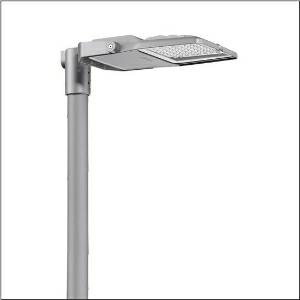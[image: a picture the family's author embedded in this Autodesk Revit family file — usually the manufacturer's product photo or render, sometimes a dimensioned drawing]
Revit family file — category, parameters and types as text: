
# Revit family: floodlight_fl_21_iq_mini___pl52_5xa7771d2d3a_64cb
name_source: partatom
category: Lighting Fixtures
units: mm (PartAtom-declared; Revit-internal decimal feet)

## family parameters
Cut with Voids When Loaded = No
Host = Face
Light Source = No
Part Type = Normal
Room Calculation Point = No
Round Connector Dimension = Use Diameter
Shared = No

## types (1)
- --- (1 x LED, 17830 lm, 143 W, 3000K)
    Apparent Load = 143 VA
    CIE Flux Codes = 26 60 98 100 100
    Color Rendering = 70
    Color Temperature = 3000K
    Default Elevation = 1800 mm
    Description = Floodlight FL 21 iQ mini, floodlight, primary light control with lens, of PMMA, primary optical cover: protective disc, of toughened safety glass, transparent, light distribution: PL52, light emission: direct distribution, installation type: surface-mounted, LED, High Power LED, rated luminous flux: 17.830lm, luminous efficacy: 125lm/W, light colour: 730, colour temperature: 3000K, control gear: iQ Comfort/DALI, control: Auto-Match, Temp-Guard, Lumen-Switch, Night-Set, Smart-Wire, Light-Fading, Desk-Remote (wireless, voltage-free reading and setting of iQ features in the workshop via application-optimized NFC function/RFID function), optimised constant luminous flux control (CLO 2.0), with terminal, 6-pole, mains connection: 220..240V, AC, 50/60Hz, start of lifetime: 143W, end of service life: 152W, reduction: 61W, luminaire housing, of diecast aluminium, powder-coated, Siteco® metallic grey (DB 702S), corrosivity category C5 mid according to DIN EN ISO 12944, suitable for swimming pools, chlorine-resistant, sealing non-destructively replaceable, please order mast flange separately, mast bracket, of steel, galvanised, powder-coated, Siteco® metallic grey (DB 702S), protection rating (complete): IP66, insulation class (complete): insulation class II (safety insulation), certification: CE, ENEC, VDE, protection symbol: D, impact resistance: IK08, permissible operating ambient temperature: -40..+40°C, permissible operating ambient temperature for outdoor applications: -40..+50°C, standard: DIN EN 12944, LABS conformity tested according to VDMA 24364:2018-05, packaging unit: 1 piece

Light Distribution: PL52
    Height = 70 mm
    Lamp = 1 x LED
    Lamp Light Flux = 17830 lm
    Lamp Power = 143 W
    Lamp count = 1
    Length = 485 mm
    Luminous efficacy = 125 lm/W
    Manufacturer = Siteco
    ModVariant = No
    Model = 5XA7771D2D3A
    Number of Poles = 1
    OnlyDefault = Yes
    Power Factor = 1
    Product Name = Floodlight FL 21 iQ mini | PL52
    Product group = floodlight | pylon annexe
    ProductGroupID = 6200
    Protection Class = Protection class II
    Protection Degree = IP 66
    RLX_Detail_Level = 1
    RLX_Emergency_Light_Flux = 0 lm
    RLX_Emergency_Type = 0
    RLX_Emergency_Type_DB = No
    RlxData = <blob elided: 101721 chars, md5=5409e721>
    Socket = socket
    Standby Power = 0 W
    System Light Flux = 17830 lm
    System Power = 143 W
    Type Comments = factory setting: luminous flux: 100 % | dim-lin: 254 | 730 mA
    Type Image = l_1007125.jpg
    URL = http://relux.com
    VarID = @adj_163978
    Voltage = 0 V
    Weight = 0.00 kg
    Width = 337 mm

## geometry (parser evidence)
native form markers: Blend x4, Sweep x12
no freeform markers — native parametric forms only
